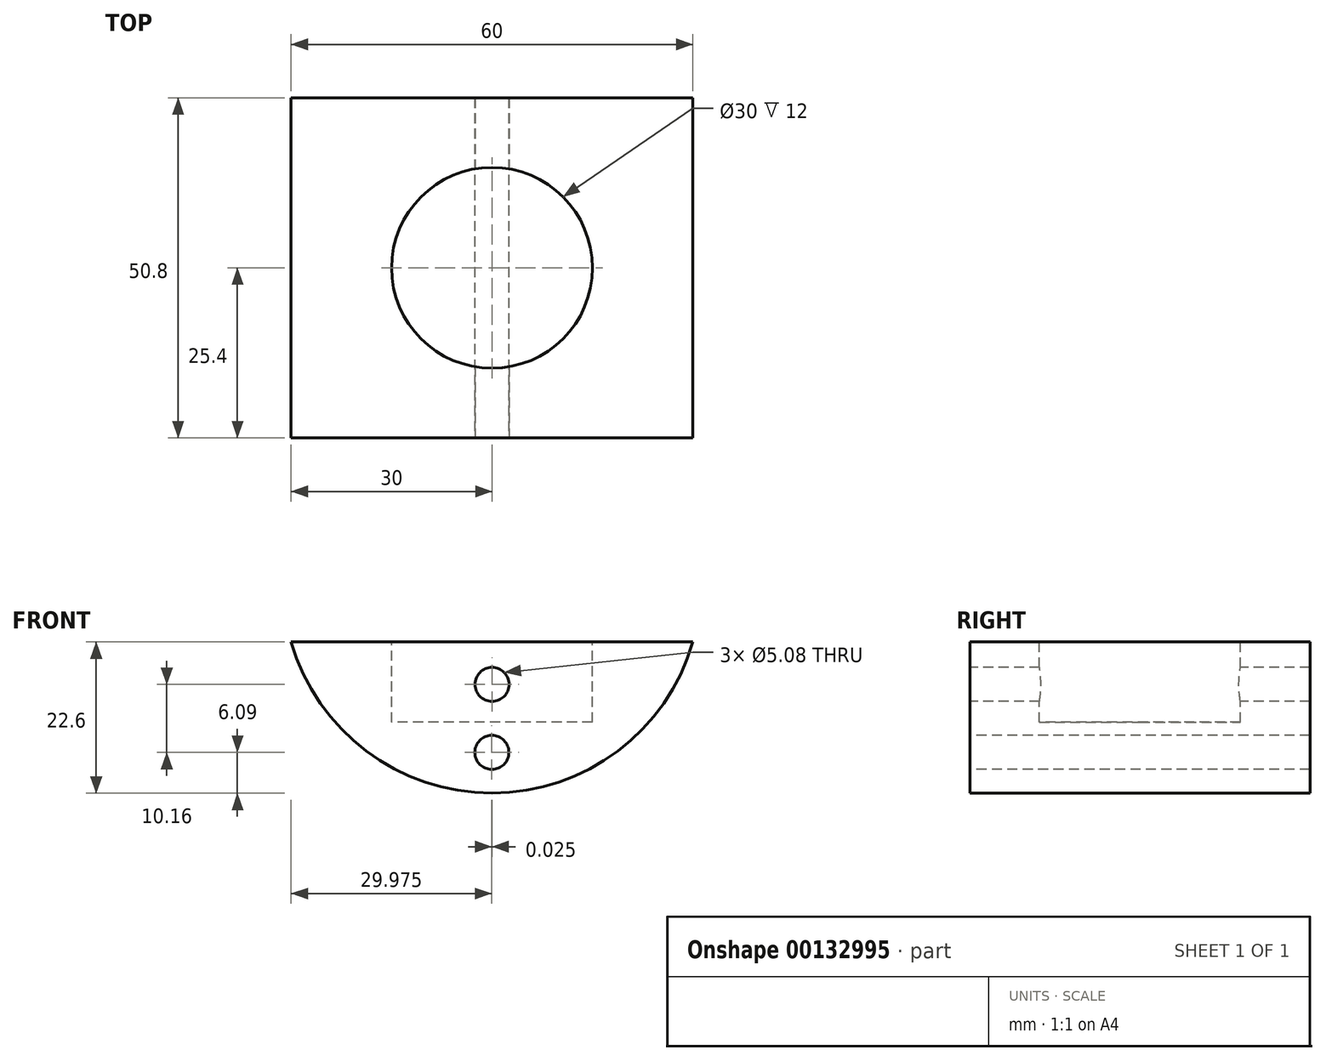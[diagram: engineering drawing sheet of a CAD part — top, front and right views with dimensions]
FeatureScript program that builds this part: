
annotation { "Feature Type Name" : "Feature", "Feature Type Description" : "" }
export const myFeature = defineFeature(function(context is Context, id is Id, definition is map)
    precondition{}
    {
        {
            var Q0;
            Q0=qCreatedBy(makeId("Front.planeOp"),FACE);
            var sketch = newSketch(context, id + "F0", { "sketchPlane" : qUnion([Q0])});
            skArc(sketch, "E0", {"start": v(-30, 0) * mm, "mid": v(0, -22.6) * mm, "end": v(30, 0) * mm});
            skLineSegment(sketch, "E1", {"start": v(-30, 0) * mm, "end": v(30, 0) * mm});
            skSolve(sketch);
        }
        {
            var Q0;
            Q0 = qSketchRegion(id + "F0", true);
            extrude(context, id + "F1", {"entities" : qUnion([Q0]), "depth" : 25.4 * mm, "hasSecondDirection" : true, "secondDirectionOppositeDirection" : true, "secondDirectionDepth" : 25.4 * mm});
        }
        {
            var Q0;
            Q0=makeQuery(id+"F1.opExtrude","SWEPT_FACE",FACE,{"disambiguationData":[OSD([sQuery(id+"F0.wireOp",EDGE,"E1")])]});
            var sketch = newSketch(context, id + "F2", { "sketchPlane" : qUnion([Q0])});
            skCircle(sketch, "E2", {"center": v(0, 0) * mm, "radius": 15 * mm});
            skSolve(sketch);
        }
        {
            var Q0;
            Q0 = qSketchRegion(id + "F2", true);
            extrude(context, id + "F3", {"entities" : qUnion([Q0]), "operationType" : NewBodyOperationType.REMOVE, "oppositeDirection" : true, "depth" : 12 * mm});
        }
        {
            var Q0;
            Q0=makeQuery(id+"F1.opExtrude","CAP_FACE",FACE,{"disambiguationData":[OSD([sQuery(id+"F0.wireOp",EDGE,"E0"),sQuery(id+"F0.wireOp",EDGE,"E1")])],"isStart":false});
            var sketch = newSketch(context, id + "F4", { "sketchPlane" : qUnion([Q0])});
            skSolve(sketch);
        }
        {
            var Q0;
            Q0=makeQuery(id+"F4.imprint","IMPRINT",FACE,{"disambiguationData":[TD([[makeQuery(id+"F4.imprint","IMPRINT",EDGE,{"derivedFrom":makeQuery(id+"F1.opExtrude","CAP_EDGE",EDGE,{"disambiguationData":[OSD([sQuery(id+"F0.wireOp",EDGE,"E0")])],"isStart":false})}),1.0]])]});
            var sketch = newSketch(context, id + "F5", { "sketchPlane" : qUnion([Q0])});
            skCircle(sketch, "E3", {"center": v(0, -6.35) * mm, "radius": 2.54 * mm});
            skCircle(sketch, "E4", {"center": v(-0.02, -16.51) * mm, "radius": 2.54 * mm});
            skSolve(sketch);
        }
        {
            var Q0;
            Q0 = qSketchRegion(id + "F5", true);
            extrude(context, id + "F6", {"entities" : qUnion([Q0]), "operationType" : NewBodyOperationType.REMOVE, "oppositeDirection" : true, "depth" : 127 * mm});
        }
    });
